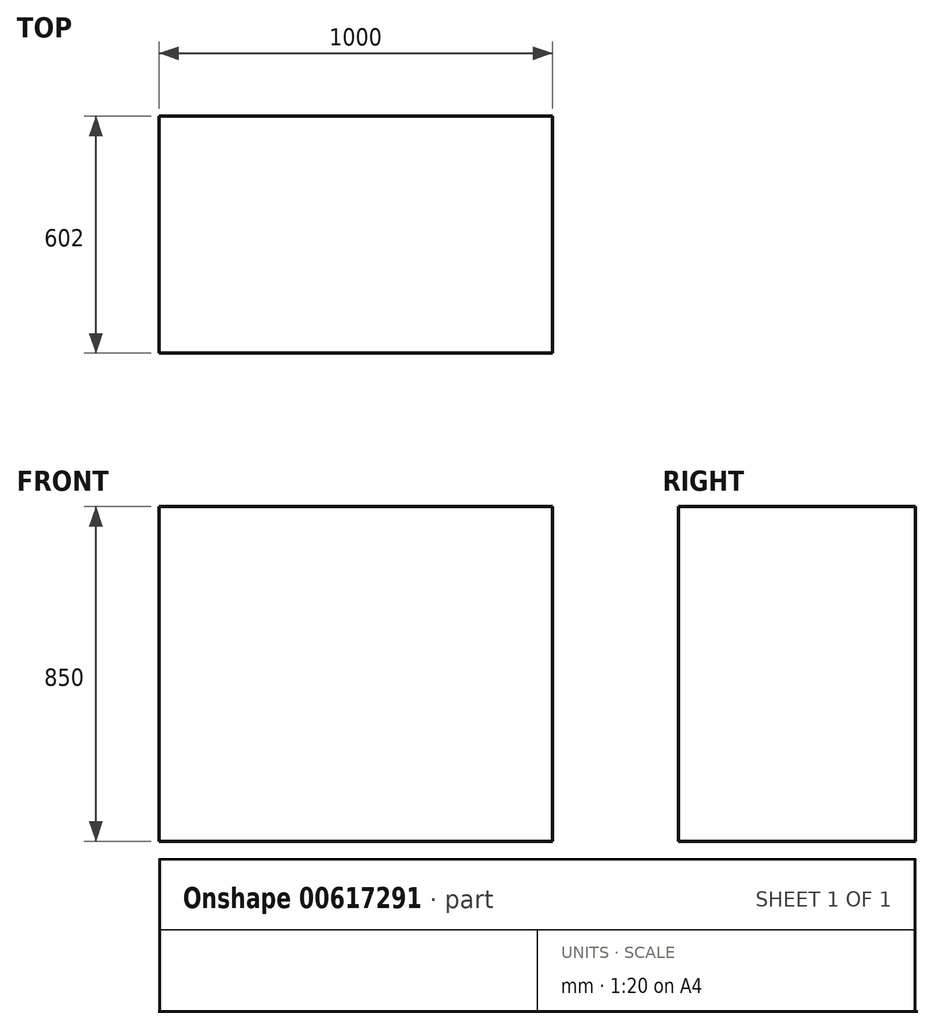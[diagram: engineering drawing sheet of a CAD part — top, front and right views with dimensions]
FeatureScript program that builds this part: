
annotation { "Feature Type Name" : "Feature", "Feature Type Description" : "" }
export const myFeature = defineFeature(function(context is Context, id is Id, definition is map)
    precondition{}
    {
        {
            var Q0;
            Q0=qCreatedBy(makeId("Top.planeOp"),FACE);
            var sketch = newSketch(context, id + "F0", { "sketchPlane" : qUnion([Q0])});
            skLineSegment(sketch, "E0.bottom", {"start": v(-497.78, 301.61) * mm, "end": v(502.22, 301.61) * mm});
            skLineSegment(sketch, "E0.top", {"start": v(-497.78, -300.39) * mm, "end": v(502.22, -300.39) * mm});
            skLineSegment(sketch, "E0.left", {"start": v(-497.78, 301.61) * mm, "end": v(-497.78, -300.39) * mm});
            skLineSegment(sketch, "E0.right", {"start": v(502.22, 301.61) * mm, "end": v(502.22, -300.39) * mm});
            skSolve(sketch);
        }
        {
            var Q0;
            Q0 = qSketchRegion(id + "F0", true);
            extrude(context, id + "F1", {"entities" : qUnion([Q0]), "depth" : 850 * mm, "offsetDistance" : 25 * mm});
        }
    });
